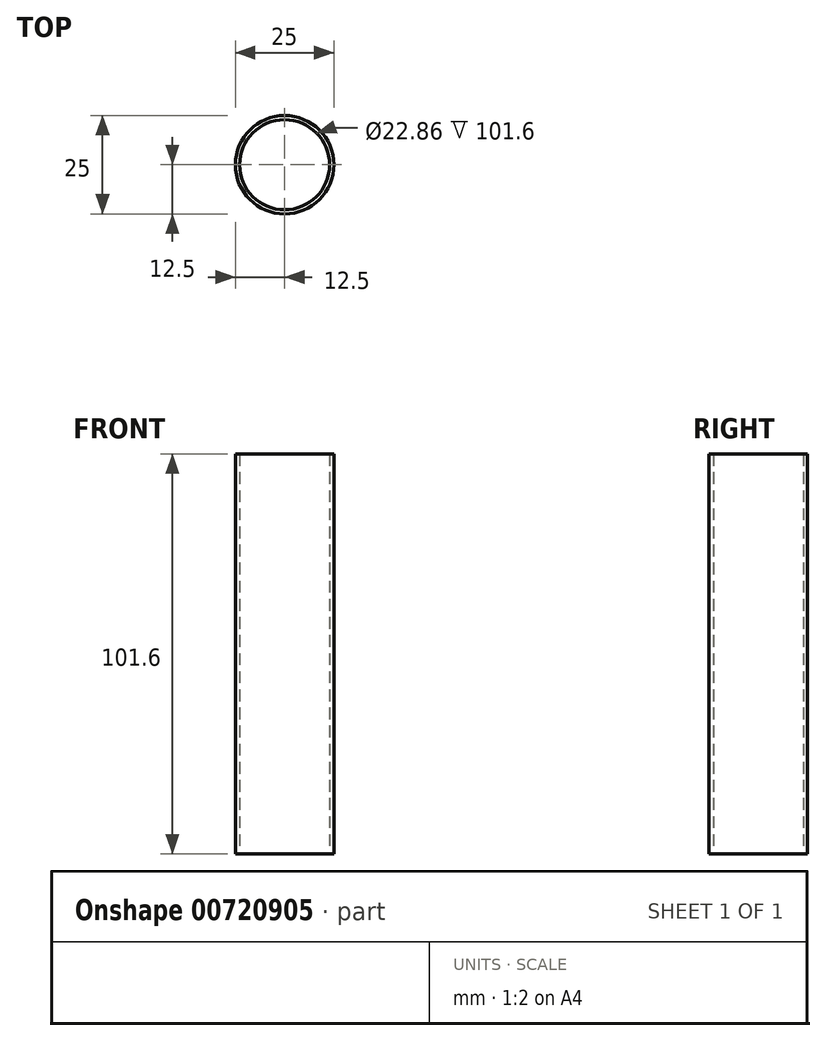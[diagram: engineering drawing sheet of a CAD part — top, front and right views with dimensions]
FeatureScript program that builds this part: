
annotation { "Feature Type Name" : "Feature", "Feature Type Description" : "" }
export const myFeature = defineFeature(function(context is Context, id is Id, definition is map)
    precondition{}
    {
        {
            var Q0;
            Q0=qCreatedBy(makeId("Top.planeOp"),FACE);
            var sketch = newSketch(context, id + "F0", { "sketchPlane" : qUnion([Q0])});
            skCircle(sketch, "E0", {"center": v(0, 0) * mm, "radius": 11.43 * mm});
            skCircle(sketch, "E1", {"center": v(0, 0) * mm, "radius": 12.5 * mm});
            skSolve(sketch);
        }
        {
            var Q0;
            Q0 = qSketchRegion(id + "F0", true);
            extrude(context, id + "F1", {"entities" : qUnion([Q0]), "depth" : 101.6 * mm, "offsetDistance" : 25.4 * mm});
        }
    });
